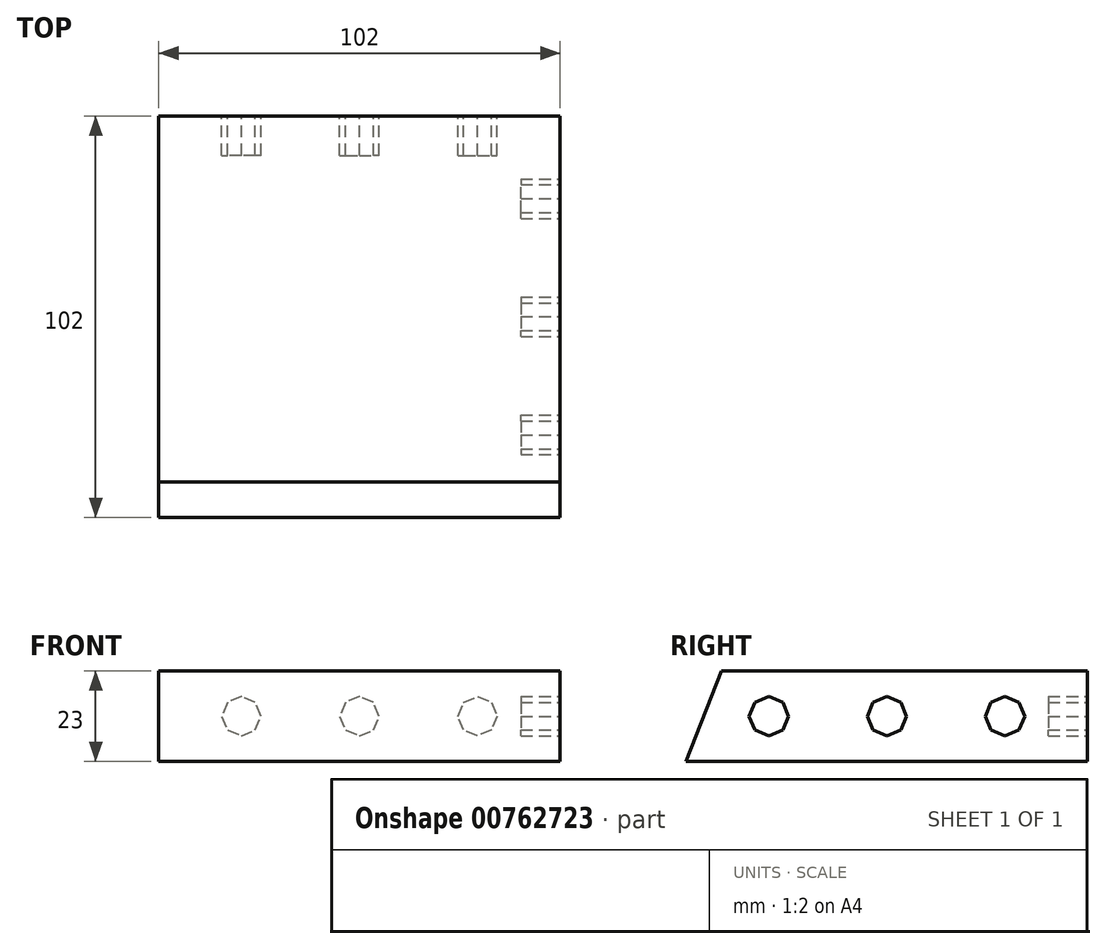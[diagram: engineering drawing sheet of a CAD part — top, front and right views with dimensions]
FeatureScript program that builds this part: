
annotation { "Feature Type Name" : "Feature", "Feature Type Description" : "" }
export const myFeature = defineFeature(function(context is Context, id is Id, definition is map)
    precondition{}
    {
        {
            var Q0;
            Q0=qCreatedBy(makeId("Right.planeOp"),FACE);
            var sketch = newSketch(context, id + "F0", { "sketchPlane" : qUnion([Q0])});
            skLineSegment(sketch, "E0.bottom", {"start": v(51, -11.5) * mm, "end": v(-51, -11.5) * mm});
            skLineSegment(sketch, "E0.top", {"start": v(51, 11.5) * mm, "end": v(-42, 11.5) * mm});
            skLineSegment(sketch, "E0.left", {"start": v(51, -11.5) * mm, "end": v(51, 11.5) * mm});
            skPoint(sketch, "E0.middle", {"position": v(0, 0) * mm});
            skLineSegment(sketch, "E1", {"start": v(-42, 11.5) * mm, "end": v(-51, -11.5) * mm});
            skPoint(sketch, "E0.right.end.orphan", {"position": v(-51, 11.5) * mm});
            skSolve(sketch);
        }
        {
            var Q0;
            Q0=qSketchRegion(id+"F0",true);
            extrude(context, id + "F1", {"entities" : qUnion([Q0]), "endBound" : BoundingType.SYMMETRIC, "depth" : 102 * mm, "offsetDistance" : 25 * mm});
        }
        {
            var Q0;
            Q0=makeQuery(id+"F1.opExtrude","SWEPT_FACE",FACE,{"disambiguationData":[OSD([sQuery(id+"F0.wireOp",EDGE,"E0.left")])]});
            var sketch = newSketch(context, id + "F2", { "sketchPlane" : qUnion([Q0])});
            skCircle(sketch, "E2.cCircle", {"center": v(0, 0) * mm, "radius": 5 * mm, "construction": true});
            skLineSegment(sketch, "E2.0", {"start": v(0, -5) * mm, "end": v(-3.54, -3.54) * mm});
            skLineSegment(sketch, "E2.1", {"start": v(-3.54, -3.54) * mm, "end": v(-5, 0) * mm});
            skLineSegment(sketch, "E2.2", {"start": v(-5, 0) * mm, "end": v(-3.54, 3.54) * mm});
            skLineSegment(sketch, "E2.3", {"start": v(-3.54, 3.54) * mm, "end": v(0, 5) * mm});
            skLineSegment(sketch, "E2.4", {"start": v(0, 5) * mm, "end": v(3.54, 3.54) * mm});
            skLineSegment(sketch, "E2.5", {"start": v(3.54, 3.54) * mm, "end": v(5, 0) * mm});
            skLineSegment(sketch, "E2.6", {"start": v(5, 0) * mm, "end": v(3.54, -3.54) * mm});
            skLineSegment(sketch, "E2.7", {"start": v(3.54, -3.54) * mm, "end": v(0, -5) * mm});
            skLineSegment(sketch, "E3.1.0.0", {"start": v(30, 5) * mm, "end": v(33.54, 3.54) * mm});
            skLineSegment(sketch, "E3.1.0.1", {"start": v(33.54, 3.54) * mm, "end": v(35, 0) * mm});
            skLineSegment(sketch, "E3.1.0.2", {"start": v(35, 0) * mm, "end": v(33.54, -3.54) * mm});
            skLineSegment(sketch, "E3.1.0.3", {"start": v(33.54, -3.54) * mm, "end": v(30, -5) * mm});
            skLineSegment(sketch, "E3.1.0.4", {"start": v(30, -5) * mm, "end": v(26.46, -3.54) * mm});
            skLineSegment(sketch, "E3.1.0.5", {"start": v(26.46, -3.54) * mm, "end": v(25, 0) * mm});
            skLineSegment(sketch, "E3.1.0.6", {"start": v(25, 0) * mm, "end": v(26.46, 3.54) * mm});
            skLineSegment(sketch, "E3.1.0.7", {"start": v(26.46, 3.54) * mm, "end": v(30, 5) * mm});
            skLineSegment(sketch, "E3.direction1", {"start": v(0, 5) * mm, "end": v(30, 5) * mm, "construction": true});
            skLineSegment(sketch, "E4.MirrorCS", {"start": v(-26.46, 3.54) * mm, "end": v(-30, 5) * mm});
            skLineSegment(sketch, "E5.MirrorCS", {"start": v(-25, 0) * mm, "end": v(-26.46, 3.54) * mm});
            skLineSegment(sketch, "E6.MirrorCS", {"start": v(-26.46, -3.54) * mm, "end": v(-25, 0) * mm});
            skLineSegment(sketch, "E7.MirrorCS", {"start": v(-30, -5) * mm, "end": v(-26.46, -3.54) * mm});
            skLineSegment(sketch, "E8.MirrorCS", {"start": v(-33.54, -3.54) * mm, "end": v(-30, -5) * mm});
            skLineSegment(sketch, "E9.MirrorCS", {"start": v(-35, 0) * mm, "end": v(-33.54, -3.54) * mm});
            skLineSegment(sketch, "E10.MirrorCS", {"start": v(-33.54, 3.54) * mm, "end": v(-35, 0) * mm});
            skLineSegment(sketch, "E11.MirrorCS", {"start": v(-30, 5) * mm, "end": v(-33.54, 3.54) * mm});
            skSolve(sketch);
        }
        {
            var Q0;
            Q0=qSketchRegion(id+"F2",true);
            extrude(context, id + "F3", {"entities" : qUnion([Q0]), "operationType" : NewBodyOperationType.REMOVE, "oppositeDirection" : true, "depth" : 10 * mm, "offsetDistance" : 25 * mm});
        }
        {
            var Q0;
            Q0=makeQuery(id+"F1.opExtrude","CAP_FACE",FACE,{"disambiguationData":[OSD([sQuery(id+"F0.wireOp",EDGE,"E0.bottom"),sQuery(id+"F0.wireOp",EDGE,"E0.left"),sQuery(id+"F0.wireOp",EDGE,"E0.top"),sQuery(id+"F0.wireOp",EDGE,"E1")])],"isStart":false});
            var sketch = newSketch(context, id + "F4", { "sketchPlane" : qUnion([Q0])});
            skCircle(sketch, "E12.cCircle", {"center": v(0, 0) * mm, "radius": 5 * mm, "construction": true});
            skLineSegment(sketch, "E12.0", {"start": v(0, -5) * mm, "end": v(-3.54, -3.54) * mm});
            skLineSegment(sketch, "E12.1", {"start": v(-3.54, -3.54) * mm, "end": v(-5, 0) * mm});
            skLineSegment(sketch, "E12.2", {"start": v(-5, 0) * mm, "end": v(-3.54, 3.54) * mm});
            skLineSegment(sketch, "E12.3", {"start": v(-3.54, 3.54) * mm, "end": v(0, 5) * mm});
            skLineSegment(sketch, "E12.4", {"start": v(0, 5) * mm, "end": v(3.54, 3.54) * mm});
            skLineSegment(sketch, "E12.5", {"start": v(3.54, 3.54) * mm, "end": v(5, 0) * mm});
            skLineSegment(sketch, "E12.6", {"start": v(5, 0) * mm, "end": v(3.54, -3.54) * mm});
            skLineSegment(sketch, "E12.7", {"start": v(3.54, -3.54) * mm, "end": v(0, -5) * mm});
            skLineSegment(sketch, "E13.1.0.0", {"start": v(30, 5) * mm, "end": v(33.54, 3.54) * mm});
            skLineSegment(sketch, "E13.1.0.1", {"start": v(26.46, 3.54) * mm, "end": v(30, 5) * mm});
            skLineSegment(sketch, "E13.1.0.2", {"start": v(25, 0) * mm, "end": v(26.46, 3.54) * mm});
            skLineSegment(sketch, "E13.1.0.3", {"start": v(26.46, -3.54) * mm, "end": v(25, 0) * mm});
            skLineSegment(sketch, "E13.1.0.4", {"start": v(30, -5) * mm, "end": v(26.46, -3.54) * mm});
            skLineSegment(sketch, "E13.1.0.5", {"start": v(33.54, -3.54) * mm, "end": v(30, -5) * mm});
            skLineSegment(sketch, "E13.1.0.6", {"start": v(35, 0) * mm, "end": v(33.54, -3.54) * mm});
            skLineSegment(sketch, "E13.1.0.7", {"start": v(33.54, 3.54) * mm, "end": v(35, 0) * mm});
            skLineSegment(sketch, "E13.direction1", {"start": v(0, 5) * mm, "end": v(30, 5) * mm, "construction": true});
            skLineSegment(sketch, "E14.MirrorCS", {"start": v(-25, 0) * mm, "end": v(-26.46, 3.54) * mm});
            skLineSegment(sketch, "E15.MirrorCS", {"start": v(-26.46, 3.54) * mm, "end": v(-30, 5) * mm});
            skLineSegment(sketch, "E16.MirrorCS", {"start": v(-30, 5) * mm, "end": v(-33.54, 3.54) * mm});
            skLineSegment(sketch, "E17.MirrorCS", {"start": v(-33.54, 3.54) * mm, "end": v(-35, 0) * mm});
            skLineSegment(sketch, "E18.MirrorCS", {"start": v(-35, 0) * mm, "end": v(-33.54, -3.54) * mm});
            skLineSegment(sketch, "E19.MirrorCS", {"start": v(-33.54, -3.54) * mm, "end": v(-30, -5) * mm});
            skLineSegment(sketch, "E20.MirrorCS", {"start": v(-30, -5) * mm, "end": v(-26.46, -3.54) * mm});
            skLineSegment(sketch, "E21.MirrorCS", {"start": v(-26.46, -3.54) * mm, "end": v(-25, 0) * mm});
            skSolve(sketch);
        }
        {
            var Q0;
            Q0 = qSketchRegion(id + "F4", true);
            extrude(context, id + "F5", {"entities" : qUnion([Q0]), "operationType" : NewBodyOperationType.REMOVE, "oppositeDirection" : true, "depth" : 10 * mm, "offsetDistance" : 25 * mm});
        }
    });
